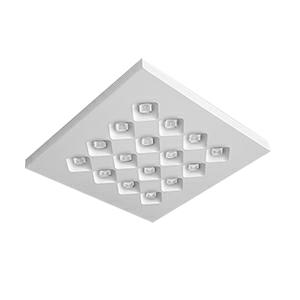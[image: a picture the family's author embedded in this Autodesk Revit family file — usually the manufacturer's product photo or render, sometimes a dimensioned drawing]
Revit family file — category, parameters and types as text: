
# Revit family: 3f_filippi_-_3f_diagon_soft_ugr_3f_filippi_-_23844_a0686_-_3f_diagon_39w-930_dali_soft_ugr_596x596___corn_plaf__d6ae
name_source: partatom
category: Lighting Fixtures
units: mm (PartAtom-declared; Revit-internal decimal feet)

## family parameters
Cut with Voids When Loaded = No
Host = Face
Light Source = No
Part Type = Normal
Room Calculation Point = No
Round Connector Dimension = Use Diameter
Shared = No

## types (1)
- 3F Filippi - 3F Dìagon Soft UGR (1 x LED, 3664 lm, 40 W, 3000 K)
    Apparent Load = 40 VA
    Approval mark = CE
    CIE Flux Codes = 59 92 100 100 100
    Color Rendering = 90
    Color Temperature = 3000 K
    Control Gear = Electronic transformer
    Default Elevation = 1800 mm
    Description = ILLUMINOTECHNICAL
Luminous efficiency 100% (DLOR 100%, ULOR 0%).
Initial luminous flux of the luminaire 3664 lm.
Direct symmetric distribution.
Installation Interdistance Transv.D = 1.23 x hu - Long.D = 1.23 x hu.
Average luminance <3000 cd/m² for radial angles >65°.
Tabular UGR (CIE 117 - 4H-8H; S=0.25H; 70/50/20): RUG 18.7 - 18.7.
Beam angle: 102° - 101°.
Luminous efficacy 92 lm/W.
Lifetime (L90/B10): 30000 h. (tq+25°C)
Lifetime (L85/B10): 50000 h. (tq+25°C)
Lifetime (L80/B20): 80000 h. (tq+25°C)
Lifetime (L70/B20): 100000 h. (tq+25°C)
Sudden decreased luminous flux after 50000 hours: 0% (C0).
Photobiological safety in compliance with IEC/TR 62778: RG0 risk exempt, (IEC 62471).
In compliance with IEC/EN 62722-2-1 - IEC/EN 62717 standards.

SOURCE
Squared LED module 39W/930.
Energy efficiency class (UE 2019/2020 - UE 2019/2015): E.
CIE 13.3 Colour rendering index: CRI >90 (R9 >50%).
IES TM-30 Fidelity Index: Rf = 92 Rg = 101.
CCT nominal colour temperature 3000 K.
Colour initial tolerance (MacAdam): SDCM 3.

MECHANICAL
Housing in hot-galvanised steel, painted in white polyester.
Honeycombed diagonal screen in white anti-glare polycarbonate.
Opal methacrylate (PMMA) rhomboid lenses with differentiated, engraved and prismatic surfaces for diffused, soft lighting and excellent visual comfort.
Luminaire with limited surface temperature. - D - (EN 60598-2-24)
Dimensions: 600x600 mm, height 40 mm. Weight 6.08 kg.
IP43 protection degree for exposed part, IP20 for recessed part.
Mechanical strength to impacts IK06 (1 joule).
Glow-wire test resistance 650°C.

ELECTRICAL
Halogen Free DALI-2, PUSH-DIM, electronic wiring 230V-50/60Hz, power factor 0.97 at full load, THD <25%, constant output current, class I, 1 driver, 1 DALI addresse.
Power of the luminaire 40 W.
ENEC - CE.
SAFE FLICKER: PstLM=<1 and SVM=<0.4 (IEC TR 61547-1 and IEC TR 63158), to ensure a more comfortable and safe light.
Luminaire compliant with EN 60598-2-22 for power supply from a centralised emergency system CPSS (Central Power Supply System), not incorporated in the luminaire - high risk areas excluded. The default power and flux are 100% in AC and 15% in DC.
Ambient temperature from 0°C to +25°C.
Temperature class T6 max 85°C.
Quick connection.
Relative humidity UR: <85%.

INSTALLATION
Ceiling.
Height only 40 mm.
All accessories dedicated to this product are available on the Catalog and on our website www.3F-Filippi.com.

ACCESSORIES
A0686 - 596x596 Diagon frame for Ceiling installation.

APPLICATIONS
Environments: staterooms, with VDTs, offices.
Environments with exacting visual tasks, where diffused soft light for optimum visual comfort is required.

LIGHT MANAGEMENT
Recommended minimum setting: 10%.
The device, equipped with DALI-2 driver, can be controlled manually with 3F Easy Dim technology or automatically/manually with 3F Smart Dimming technology and/or centralised DALI systems.
DALI-2 certification guarantees interoperability with other devices with the same certification.
In electrical systems without a regulation system (manual or automatic) and DALI bus, a suitable jumper must be made on the DA-DA terminals of the appliance.

WARNING
Luminaire designed for disposal/recycling at end-of-life.
Replaceable (LED only) light source by a professional. Replaceable control gear by a professional.
    Height = 0 mm  [stored 0 ft]
    Lamp = 1 x LED
    Lamp Light Flux = 3664 lm
    Lamp Power = 40 W
    Lamp count = 1
    Length = 600 mm
    Lifetime = 50000 h
    Luminous efficacy = 92 lm/W
    Manufacturer = 3F Filippi
    ModVariant = No
    Model = 3F Filippi - 23844+A0686 - 3F Diagon 39W-930 DALI SOFT UGR 596x596 + Corn.plaf.
    Mounting Place = Ceiling
    Mounting Type = Recessed
    Number of Poles = 1
    OnlyDefault = Yes
    Power Factor = 1
    Product Name = 3F Filippi - 3F Dìagon Soft UGR
    Product group = recessed luminaire
    ProductGroupID = 4
    Protection Class = Protection class I
    Protection Degree = IP 20
    RLX_Detail_Level = 1
    RLX_Emergency_Light_Flux = 0 lm
    RLX_Emergency_Type = 0
    RLX_Emergency_Type_DB = No
    RlxData = <blob elided: 97641 chars, md5=970ead7f>
    Socket = socket
    Standby Power = 0 W
    System Light Flux = 3664 lm
    System Power = 40 W
    Type Comments = Product without accessories
    Type Image = 3ffilippi_3f_diagon__a0686.jpg
    URL = http://relux.com
    VarID = ---
    Voltage = 0 V
    Weight = 0.00 kg
    Width = 600 mm

note: [stored X ft] marks values corroborated as IEEE doubles in the binary element streams (Revit-internal decimal feet)

## geometry (parser evidence)
native form markers: Blend x4, Sweep x10
no freeform markers — native parametric forms only
